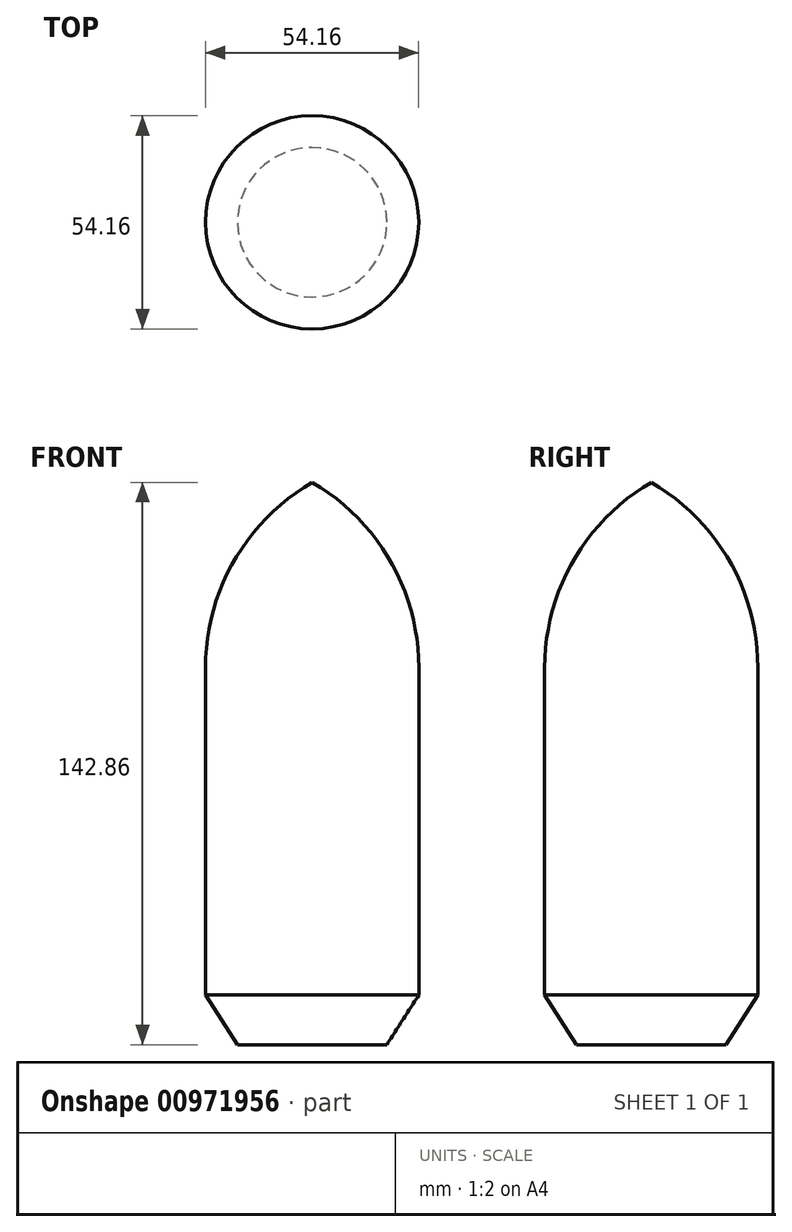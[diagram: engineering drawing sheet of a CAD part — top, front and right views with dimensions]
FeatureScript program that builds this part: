
annotation { "Feature Type Name" : "Feature", "Feature Type Description" : "" }
export const myFeature = defineFeature(function(context is Context, id is Id, definition is map)
    precondition{}
    {
        {
            var Q0;
            Q0=qCreatedBy(makeId("Front.planeOp"),FACE);
            var sketch = newSketch(context, id + "F0", { "sketchPlane" : qUnion([Q0])});
            skLineSegment(sketch, "E0", {"start": v(0, 0) * mm, "end": v(0, 79.28) * mm});
            skLineSegment(sketch, "E1", {"start": v(0, 79.28) * mm, "end": v(0, -63.58) * mm});
            skLineSegment(sketch, "E2", {"start": v(0, -63.58) * mm, "end": v(-18.98, -63.58) * mm});
            skLineSegment(sketch, "E3", {"start": v(-18.98, -63.58) * mm, "end": v(-27.08, -50.96) * mm});
            skLineSegment(sketch, "E4", {"start": v(-27.08, -50.96) * mm, "end": v(-27.08, 32.25) * mm});
            skArc(sketch, "E5", {"start": v(0, 79.28) * mm, "mid": v(-19.83, 59.38) * mm, "end": v(-27.08, 32.25) * mm});
            skSolve(sketch);
        }
        {
            var Q0;
            {var subQ0=sQuery(id+"F0.wireOp",EDGE,"E2");Q0=makeQuery(id+"F0.imprint","IMPRINT",FACE,{"disambiguationData":[TD([[makeQuery(id+"F0.imprint","IMPRINT",EDGE,{"derivedFrom":subQ0}),-1.0]])]});}
            var Q1;
            Q1=sQuery(id+"F0.wireOp",EDGE,"E1");
            revolve(context, id + "F1", {"surfaceOperationType" : NewSurfaceOperationType.NEW, "entities" : qUnion([Q0]), "axis" : qUnion([Q1]), "revolveType" : RevolveType.FULL});
        }
    });
